# Revit family: E_FF108 Cable Basket Sleeve
name_source: partatom
category: Specialty Equipment
revit_build: Autodesk Revit 2015 (Build: 20160512_0715(x64)
units: mm (PartAtom-declared; Revit-internal decimal feet)

## types (8) — shared parameters
Height = 54 mm  [stored 0.177165 ft]
IFC Classification = Building Element Proxy
Length = 180 mm  [stored 0.590551 ft]
Manufacturer = Tenmat ltd
Material = Intumescent Sealant
Performance = BS EN 1366-3:2009 & BS 476, ETA-12/0332, 1224-CPR-0341, CE Marked
Type Comments = To be filled with 20 x 180mm Infill sheet supplied at 1000m Lengths
URL = https://www.tenmat.com

## per-type parameters (varying)
| type | Description | Width |
| 75 x 54mm | FireFly 108 75x54mm Cable Basket sleeve | 75 mm |
| 100 x 54mm | FireFly 108 100x54mm Cable Basket sleeve | 100 mm  [stored 0.328084 ft] |
| 150 x 54mm | FireFly 108 150x54mm Cable Basket sleeve | 150 mm |
| 200 x 54mm | FireFly 108 200x54mm Cable Basket sleeve | 200 mm  [stored 0.656168 ft] |
| 250 x 54mm | FireFly 108 250x54mm Cable Basket sleeve | 250 mm  [stored 0.82021 ft] |
| 300 x 54mm | FireFly 108 300x54mm Cable Basket sleeve | 300 mm |
| 400 x 54mm | FireFly 108 400x54mm Cable Basket sleeve | 400 mm  [stored 1.31234 ft] |
| 450 x 54mm | FireFly 108 450x54mm Cable Basket sleeve | 450 mm  [stored 1.47638 ft] |

note: [stored X ft] marks values corroborated as IEEE doubles in the binary element streams (Revit-internal decimal feet)

## geometry (parser evidence)
native form markers: Blend x2, Sweep x3
no freeform markers — native parametric forms only
